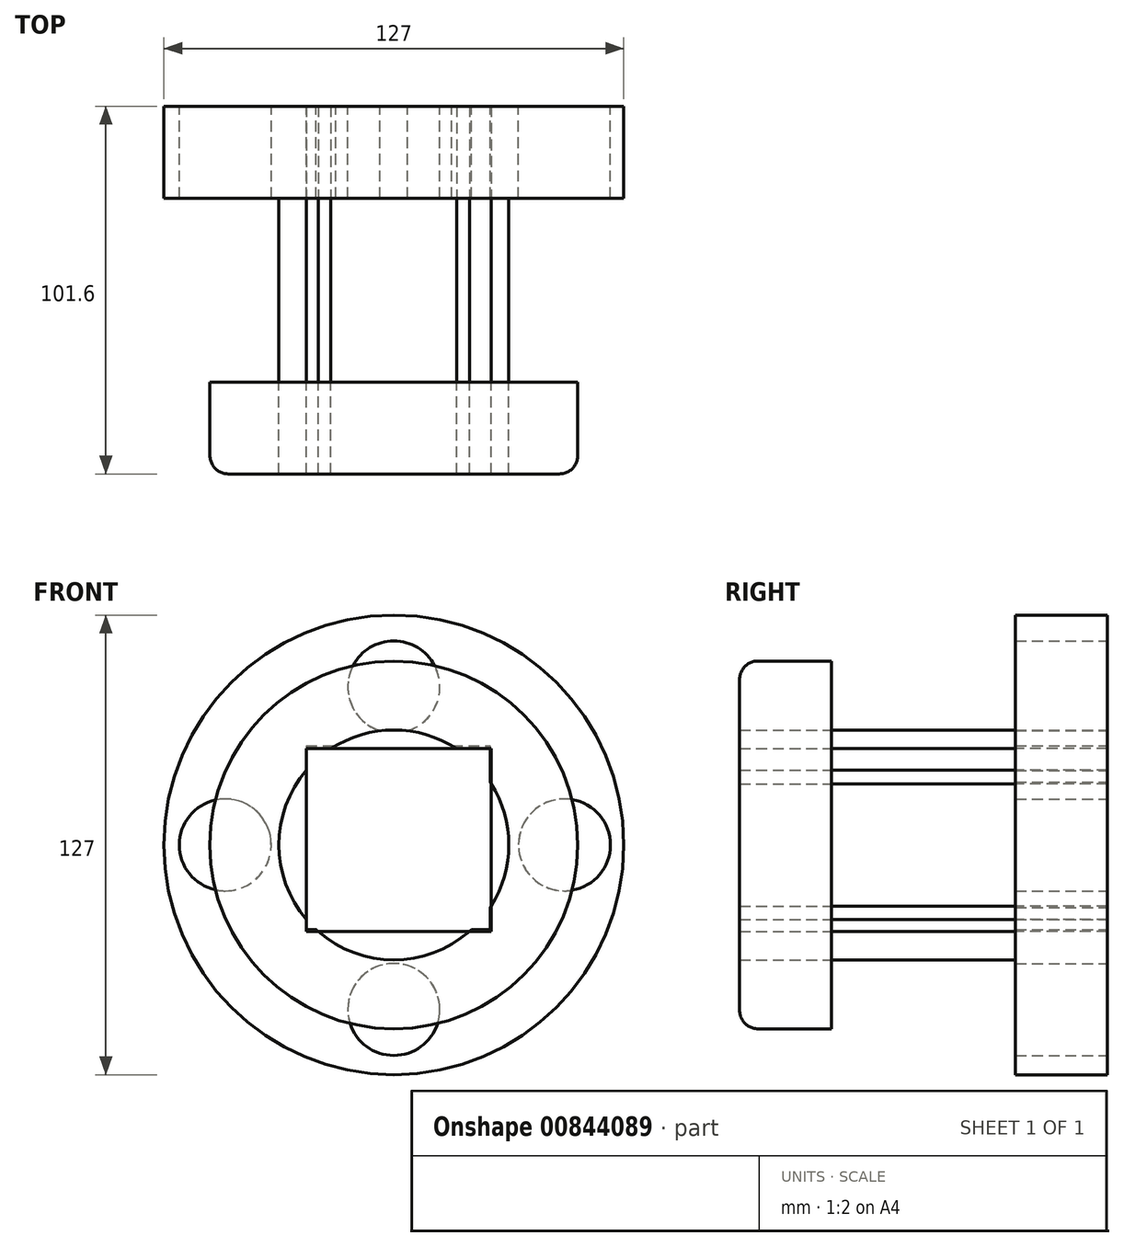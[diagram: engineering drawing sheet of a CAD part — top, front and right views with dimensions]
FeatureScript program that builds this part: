
annotation { "Feature Type Name" : "Feature", "Feature Type Description" : "" }
export const myFeature = defineFeature(function(context is Context, id is Id, definition is map)
    precondition{}
    {
        {
            var Q0;
            Q0=qCreatedBy(makeId("Front.planeOp"),FACE);
            var sketch = newSketch(context, id + "F0", { "sketchPlane" : qUnion([Q0])});
            skCircle(sketch, "E0", {"center": v(0, 0) * mm, "radius": 63.5 * mm});
            skLineSegment(sketch, "E1.bottom", {"start": v(20.15, -15.37) * mm, "end": v(20.15, -15.37) * mm});
            skLineSegment(sketch, "E1.top", {"start": v(20.15, -27.02) * mm, "end": v(20.15, -27.02) * mm});
            skLineSegment(sketch, "E2", {"start": v(-24.19, 27.4) * mm, "end": v(-24.19, -23.4) * mm});
            skLineSegment(sketch, "E3", {"start": v(-24.19, -23.4) * mm, "end": v(26.61, -23.4) * mm});
            skLineSegment(sketch, "E4", {"start": v(26.61, -23.4) * mm, "end": v(26.61, 27.4) * mm});
            skLineSegment(sketch, "E5", {"start": v(-24.19, 27.4) * mm, "end": v(26.61, 27.4) * mm});
            skCircle(sketch, "E6", {"center": v(0, -45.47) * mm, "radius": 12.7 * mm});
            skCircle(sketch, "E7", {"center": v(-46.57, 0) * mm, "radius": 12.7 * mm});
            skCircle(sketch, "E8", {"center": v(0, 43.65) * mm, "radius": 12.7 * mm});
            skCircle(sketch, "E9", {"center": v(47.14, 0) * mm, "radius": 12.7 * mm});
            skSolve(sketch);
        }
        {
            var Q0;
            Q0=makeQuery(id+"F0.imprint","IMPRINT",FACE,{"disambiguationData":[TD([[makeQuery(id+"F0.imprint","IMPRINT",EDGE,{"derivedFrom":sQuery(id+"F0.wireOp",EDGE,"E0")}),1.0]])]});
            extrude(context, id + "F1", {"entities" : qUnion([Q0]), "depth" : 25.4 * mm, "offsetDistance" : 25.4 * mm});
        }
        {
            var Q0;
            Q0=qCreatedBy(makeId("Front.planeOp"),FACE);
            var sketch = newSketch(context, id + "F2", { "sketchPlane" : qUnion([Q0])});
            skCircle(sketch, "E10", {"center": v(0, 0) * mm, "radius": 31.75 * mm});
            skSolve(sketch);
        }
        {
            var Q0;
            Q0=makeQuery(id+"F2.imprint","IMPRINT",FACE,{"disambiguationData":[TD([[makeQuery(id+"F2.imprint","IMPRINT",EDGE,{"derivedFrom":sQuery(id+"F2.wireOp",EDGE,"E10")}),1.0]])]});
            extrude(context, id + "F3", {"entities" : qUnion([Q0]), "operationType" : NewBodyOperationType.ADD, "depth" : 76.2 * mm, "offsetDistance" : 25.4 * mm});
        }
        {
            var Q0;
            Q0=makeQuery(id+"F3.opExtrude","CAP_FACE",FACE,{"disambiguationData":[OSD([sQuery(id+"F2.wireOp",EDGE,"E10")])],"isStart":false});
            var sketch = newSketch(context, id + "F4", { "sketchPlane" : qUnion([Q0])});
            skCircle(sketch, "E11", {"center": v(0, 0) * mm, "radius": 50.8 * mm});
            skLineSegment(sketch, "E12", {"start": v(-24.16, 26.57) * mm, "end": v(-24.16, -23.93) * mm});
            skLineSegment(sketch, "E13", {"start": v(-24.16, -23.93) * mm, "end": v(26.88, -23.93) * mm});
            skLineSegment(sketch, "E14", {"start": v(26.88, -23.93) * mm, "end": v(26.88, 26.57) * mm});
            skLineSegment(sketch, "E15", {"start": v(-24.16, 26.57) * mm, "end": v(26.88, 26.57) * mm});
            skSolve(sketch);
        }
        {
            var Q0;
            Q0=makeQuery(id+"F4.imprint","IMPRINT",FACE,{"disambiguationData":[TD([[makeQuery(id+"F4.imprint","IMPRINT",EDGE,{"derivedFrom":sQuery(id+"F4.wireOp",EDGE,"E11")}),1.0]])]});
            var sketch = newSketch(context, id + "F5", { "sketchPlane" : qUnion([Q0])});
            skSolve(sketch);
        }
        {
            var Q0;
            Q0=makeQuery(id+"F5.imprint","IMPRINT",FACE,{"disambiguationData":[TD([[makeQuery(id+"F5.imprint","IMPRINT",EDGE,{"derivedFrom":makeQuery(id+"F4.imprint","IMPRINT",EDGE,{"derivedFrom":sQuery(id+"F4.wireOp",EDGE,"E11")})}),1.0]])]});
            extrude(context, id + "F6", {"entities" : qUnion([Q0]), "depth" : 25.4 * mm, "offsetDistance" : 25.4 * mm});
        }
        {
            var Q0;
            {var subQ1=makeQuery(id+"F3.opExtrude","CAP_EDGE",EDGE,{"disambiguationData":[OSD([sQuery(id+"F2.wireOp",EDGE,"E10")])],"isStart":false});var subQ10=sQuery(id+"F4.wireOp",EDGE,"E12");var subQ11=makeQuery(id+"F4.imprint","INTERSECT",VERTEX,{"disambiguationData":[OD(0.0)],"derivedFrom":[subQ1,subQ10]});Q0=makeQuery(id+"F4.imprint","IMPRINT",FACE,{"disambiguationData":[TD([[makeQuery(id+"F4.imprint","IMPRINT",EDGE,{"disambiguationData":[TD([[subQ11,-1.0]])],"derivedFrom":subQ10}),1.0]])]});}
            extrude(context, id + "F7", {"entities" : qUnion([Q0]), "operationType" : NewBodyOperationType.REMOVE, "oppositeDirection" : true, "depth" : 76.2 * mm, "offsetDistance" : 25.4 * mm});
        }
        {
            var Q0;
            Q0=makeQuery(id+"F6.opExtrude","CAP_EDGE",EDGE,{"disambiguationData":[OSD([sQuery(id+"F4.wireOp",EDGE,"E11")])],"isStart":false});
            fillet(context, id + "F8", {"entities" : qUnion([Q0]), "radius" : 5.08 * mm, "tangentPropagation" : true, "allowEdgeOverflow" : false});
        }
    });
